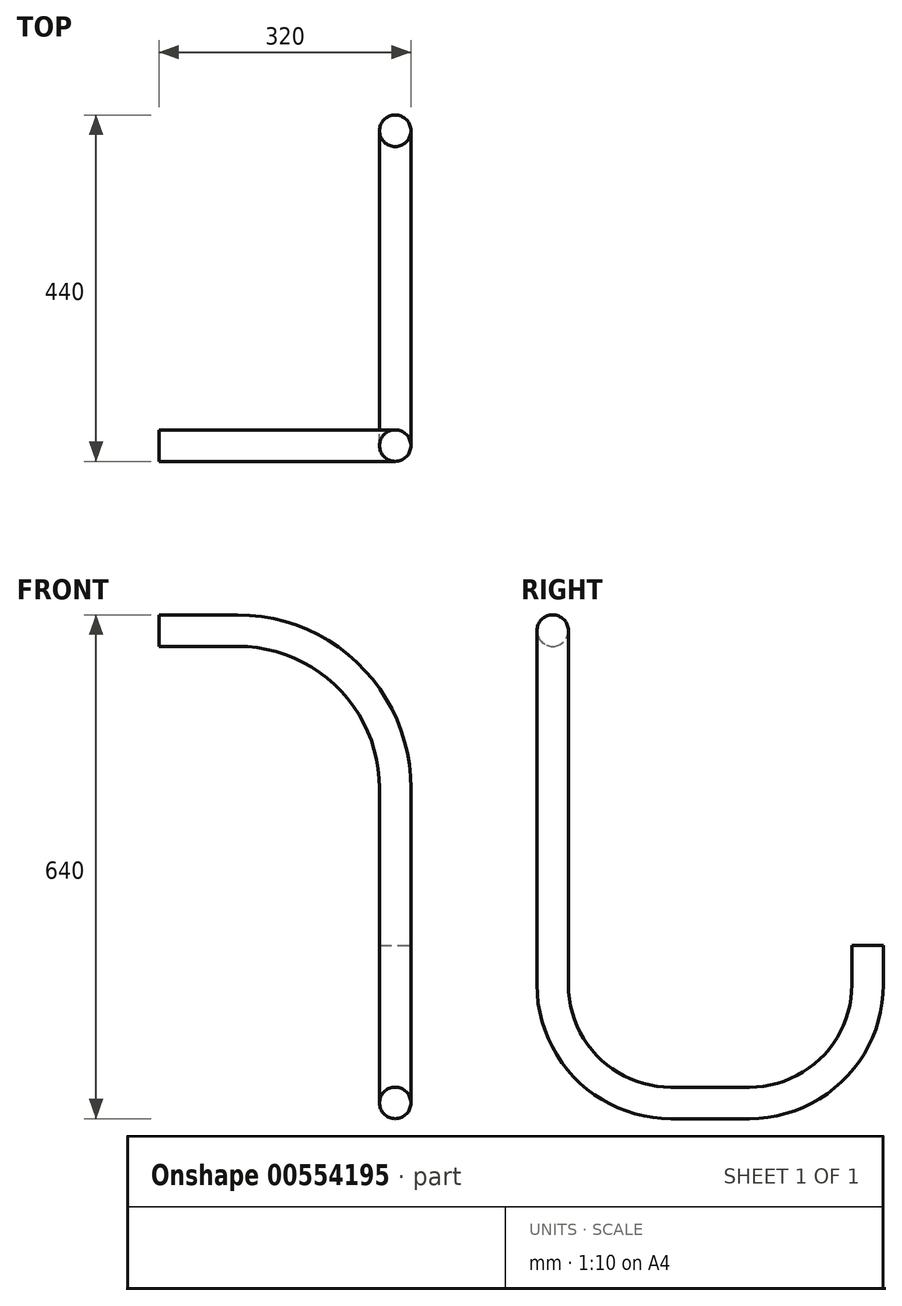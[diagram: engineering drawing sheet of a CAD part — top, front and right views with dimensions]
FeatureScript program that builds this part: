
annotation { "Feature Type Name" : "Feature", "Feature Type Description" : "" }
export const myFeature = defineFeature(function(context is Context, id is Id, definition is map)
    precondition{}
    {
        {
            var Q0;
            Q0=qCreatedBy(makeId("Front.planeOp"),FACE);
            var sketch = newSketch(context, id + "F0", { "sketchPlane" : qUnion([Q0])});
            skLineSegment(sketch, "E0", {"start": v(0, 0) * mm, "end": v(100, 0) * mm});
            skLineSegment(sketch, "E1", {"start": v(300, -200) * mm, "end": v(300, -600) * mm});
            skPoint(sketch, "E2.visualSharp", {"position": v(300, 0) * mm});
            skArc(sketch, "E2.filletArc", {"start": v(300, -200) * mm, "mid": v(241.42, -58.58) * mm, "end": v(100, 0) * mm});
            skSolve(sketch);
        }
        {
            var Q0;
            Q0=qCreatedBy(makeId("Right.planeOp"),FACE);
            var Q1;
            Q1=sQuery(id+"F0.wireOp",VERTEX,"E1.end");
            cPlane(context, id + "F1", {"entities" : qUnion([Q0, Q1]), "cplaneType" : CPlaneType.PLANE_POINT, "offset" : 25 * mm, "width" : 150 * mm, "height" : 150 * mm});
        }
        {
            var Q0;
            Q0=qCreatedBy(id+"F1.planeOp",FACE);
            var sketch = newSketch(context, id + "F2", { "sketchPlane" : qUnion([Q0])});
            skPoint(sketch, "E3.0", {"position": v(0, -600) * mm});
            skLineSegment(sketch, "E4.0", {"start": v(0, -200) * mm, "end": v(0, -450) * mm});
            skLineSegment(sketch, "E5", {"start": v(150, -600) * mm, "end": v(250, -600) * mm});
            skLineSegment(sketch, "E6", {"start": v(400, -450) * mm, "end": v(400, -400) * mm});
            skArc(sketch, "E7.filletArc", {"start": v(0, -450) * mm, "mid": v(43.93, -556.07) * mm, "end": v(150, -600) * mm});
            skPoint(sketch, "E8.visualSharp", {"position": v(400, -600) * mm});
            skArc(sketch, "E8.filletArc", {"start": v(250, -600) * mm, "mid": v(356.07, -556.07) * mm, "end": v(400, -450) * mm});
            skSolve(sketch);
        }
        {
            var Q0;
            Q0=qCreatedBy(makeId("Right.planeOp"),FACE);
            var sketch = newSketch(context, id + "F3", { "sketchPlane" : qUnion([Q0])});
            skCircle(sketch, "E9", {"center": v(0, 0) * mm, "radius": 20 * mm});
            skSolve(sketch);
        }
        {
            var Q0;
            Q0=makeQuery(id+"F3.imprint","IMPRINT",FACE,{"disambiguationData":[TD([[makeQuery(id+"F3.imprint","IMPRINT",EDGE,{"derivedFrom":sQuery(id+"F3.wireOp",EDGE,"E9")}),1.0]])]});
            var Q1;
            Q1=sQuery(id+"F0.wireOp",EDGE,"E0");
            var Q2;
            Q2=sQuery(id+"F0.wireOp",EDGE,"E2.filletArc");
            var Q3;
            Q3=sQuery(id+"F2.wireOp",EDGE,"E4.0");
            var Q4;
            Q4=sQuery(id+"F2.wireOp",EDGE,"E7.filletArc");
            var Q5;
            Q5=sQuery(id+"F2.wireOp",EDGE,"E5");
            var Q6;
            Q6=sQuery(id+"F2.wireOp",EDGE,"E8.filletArc");
            var Q7;
            Q7=sQuery(id+"F2.wireOp",EDGE,"E6");
            sweep(context, id + "F4", {"profiles" : qUnion([Q0]), "path" : qUnion([Q1, Q2, Q3, Q4, Q5, Q6, Q7])});
        }
    });
